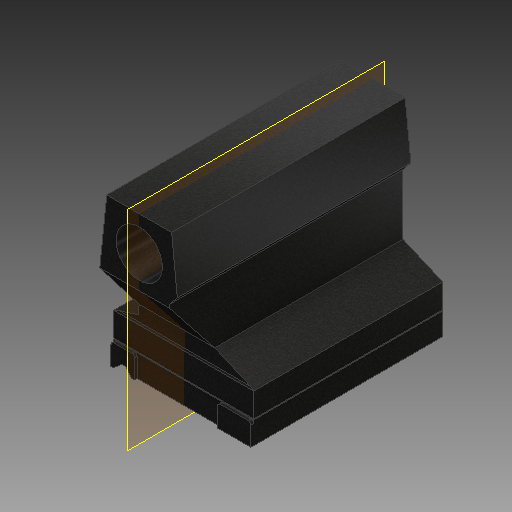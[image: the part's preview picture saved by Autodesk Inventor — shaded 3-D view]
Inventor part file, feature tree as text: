
AUTODESK INVENTOR PART (.ipt)
format: ipt  version: 2018 (Build 220112000, 112)  size: 501,248 bytes
history: native  units: mm
features: extrude x26, sketch x26, fillet x6, plane x2
ambient origin geometry x8: Origin, YZ Plane, XZ Plane, XY Plane, X Axis, Y Axis, Z Axis, Center Point
bodies: Solid1 (feature_tree)
feature tree (60):
  extrude  "Extrusion1"  Depth=151.0mm
  extrude  "Extrusion2"  Depth=203.0mm
  extrude  "Extrusion3"  TaperAngle=135.0deg  [1 undecoded]
  extrude  "Extrusion4"  Depth=10.0mm
  extrude  "Extrusion5"  Depth=28.0mm
  extrude  "Extrusion6"  Depth=2.0mm TaperAngle=0.0deg
  fillet  "Fillet1"  Radius=37.0mm
  extrude  "Extrusion7"  Depth=1.0mm TaperAngle=0.0deg
  fillet  "Fillet3"  Radius=5.0mm
  extrude  "Extrusion8"  Depth=5.0mm
  extrude  "Extrusion9"  Depth=1.0mm
  extrude  "Extrusion10"  Depth=1.0mm
  extrude  "Extrusion11"  Depth=1.0mm TaperAngle=0.0deg
  plane  "Work Plane1"
  extrude  "Extrusion12"  Depth=49.0mm TaperAngle=0.0deg
  extrude  "Extrusion13"  Depth=35.0mm
  extrude  "Extrusion14"  Depth=16.755161mm
  extrude  "Extrusion15"  Depth=295.5mm TaperAngle=0.0deg
  fillet  "Fillet4"  Radius=295.5mm
  extrude  "Extrusion16"  Depth=295.5mm TaperAngle=0.0deg
  extrude  "Extrusion17"  Depth=2.0mm
  plane  "Work Plane2"
  extrude  "Extrusion18"  Depth=50.0mm
  extrude  "Extrusion19"  Depth=5.0mm TaperAngle=0.0deg
  extrude  "Extrusion20"  Depth=1.0mm TaperAngle=0.0deg
  extrude  "Extrusion21"  Depth=207.0mm TaperAngle=0.0deg
  extrude  "Extrusion22"  Depth=204.0mm
  extrude  "Extrusion23"  Depth=6.981317mm
  extrude  "Extrusion24"  Depth=204.0mm TaperAngle=0.0deg
  fillet  "Fillet5"  Radius=25.3mm
  fillet  "Fillet6"  Radius=3.0mm
  extrude  "Extrusion25"  Depth=3.0mm
  fillet  "Fillet7"  Radius=36.2mm
  extrude  "Extrusion26"  Depth=3.0mm
  sketch  "Sketch1"  dims[d19=26.0mm d20=151.0mm]
  sketch  "Sketch2"  dims[d21=203.0mm d22=0.0mm d23=28.0mm]
  sketch  "Sketch3"  dims[d29=4.0mm d30=135.0deg]
  sketch  "Sketch4"  dims[d31=45.0deg d32=10.0mm]
  sketch  "Sketch5"  dims[d33=215.0mm d34=0.0mm d35=28.0mm]
  sketch  "Sketch6"  dims[d36=6.0mm d37=0.0mm d38=2.0mm d39=0.0mm d40=37.0mm]
  sketch  "Sketch8"  dims[d41=6.0mm d42=0.0mm d43=1.0mm d44=0.0mm d45=5.0mm]
  sketch  "Sketch9"  dims[d47=1.0mm d48=0.0mm d49=5.0mm]
  sketch  "Sketch10"  dims[d50=1.0mm d51=1.0mm]
  sketch  "Sketch11"  dims[d52=1.0mm d53=1.0mm]
  sketch  "Sketch12"  dims[d54=1.0mm d55=0.0mm d56=26.0mm d57=0.0mm]
  sketch  "Sketch13"  dims[d58=49.0mm d59=152.0mm d60=0.0mm]
  sketch  "Sketch14"  dims[d61=35.0mm d62=35.0mm]
  sketch  "Sketch15"  dims[d63=16.755161mm d64=16.755161mm]
  sketch  "Sketch16"  dims[d65=58.0mm d66=295.5mm d67=0.0mm d68=295.5mm d69=0.0mm]
  sketch  "Sketch18"  dims[d70=295.5mm d71=0.0mm d72=295.5mm d73=0.0mm]
  sketch  "Sketch19"  dims[d74=1.0mm d75=0.0mm d76=2.0mm]
  sketch  "Sketch20"  dims[d85=1.0mm d86=0.0mm d87=50.0mm]
  sketch  "Sketch21"  dims[d88=300.0mm d89=0.0mm d90=5.0mm d91=0.0mm]
  sketch  "Sketch23"  dims[d92=1.0mm d93=0.0mm d94=1.0mm d95=0.0mm]
  sketch  "Sketch24"  dims[d96=2.0mm d97=207.0mm d98=0.0mm]
  sketch  "Sketch25"  dims[d99=204.0mm d100=0.0mm d101=148.124mm]
  sketch  "Sketch26"  dims[d102=10.2mm d103=6.981317mm]
  sketch  "Sketch27"  dims[d104=3.8mm d106=204.0mm d107=0.0mm d108=25.3mm d109=3.0mm d110=0.0mm]
  sketch  "Sketch28"  dims[d111=3.0mm d112=3.0mm d113=36.2mm]
  sketch  "Sketch29"  dims[d114=3.0mm d115=0.0mm d116=3.0mm d117=2.0mm d118=24.43461mm d121=4.0mm d122=8.0mm d123=22.68928mm d124=10.0mm d125=0.0mm]
note: 1 required parameter value undecoded (feature->parameter linkage not recoverable at this tier; creation-order binding heuristic only, values carry confidence <= 0.55)
